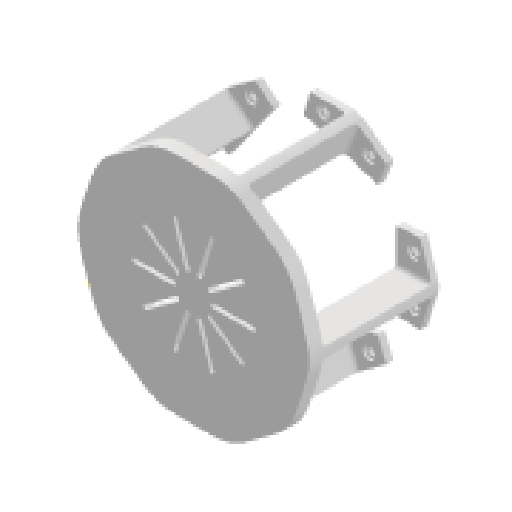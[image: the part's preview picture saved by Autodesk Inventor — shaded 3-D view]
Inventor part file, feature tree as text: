
AUTODESK INVENTOR PART (.ipt)
format: ipt  version: 2025 (Build 290162000, 162)  size: 346,112 bytes
history: native  units: mm
features: extrude x6, sketch x6, fillet x3, pattern_circular x3, other x3, reference x2, plane x1
ambient origin geometry x8: Origin, YZ Plane, XZ Plane, XY Plane, X Axis, Y Axis, Z Axis, Center Point
bodies: Solid1 (feature_tree)
feature tree (24):
  extrude  "Extrusion1"  Depth=0.436332mm
  plane  "Work Plane1"
  extrude  "Extrusion2"  Depth=83.0mm TaperAngle=0.0deg
  extrude  "Extrusion3"  Depth=2.0mm TaperAngle=0.0deg
  fillet  "Fillet1"  Radius=5.0mm
  extrude  "Extrusion4"  Depth=25.4mm
  fillet  "Fillet2"  Radius=3.0mm
  pattern_circular  "Circular Pattern2"  [2 undecoded]
  extrude  "Extrusion5"  Depth=40.0mm TaperAngle=360.0deg
  pattern_circular  "Circular Pattern3"  [2 undecoded]
  extrude  "Extrusion6"  Depth=40.0mm TaperAngle=360.0deg
  pattern_circular  "Circular Pattern4"  [2 undecoded]
  fillet  "Fillet3"  Radius=9.0mm
  sketch  "Sketch1"  dims[d0=6.0mm d1=0.436332mm]
  reference  "Reference1"
  sketch  "Sketch2"  dims[d2=0.436332mm d3=83.0mm d4=0.0mm]
  sketch  "Sketch3"  dims[d8=10.0mm d9=0.0mm d10=2.0mm d11=0.0mm d13=5.0mm d14=0.0mm]
  reference  "Reference3"
  sketch  "Sketch4"  dims[d15=25.4mm d16=25.4mm d19=3.0mm]
  sketch  "Sketch5"  dims[d20=3.0mm]
  sketch  "Sketch6"  dims[d21=5.5mm d22=5.5mm d23=50.0mm d24=360.0deg d26=5.0mm d27=0.0mm d28=100.0mm d29=360.0deg d31=9.0mm d32=9.0mm d33=2.0mm d34=0.0mm d35=50.0mm d36=360.0deg d38=40.0mm d39=0.0mm d40=0.0mm d41=0.0mm]
  other  "<userpath>\Desktop\puppycat\liarAssembly.iam"
  other  "liarAssembly.iam"
  other  "lidarCage:1"
note: 6 required parameter values undecoded (feature->parameter linkage not recoverable at this tier; creation-order binding heuristic only, values carry confidence <= 0.55)
